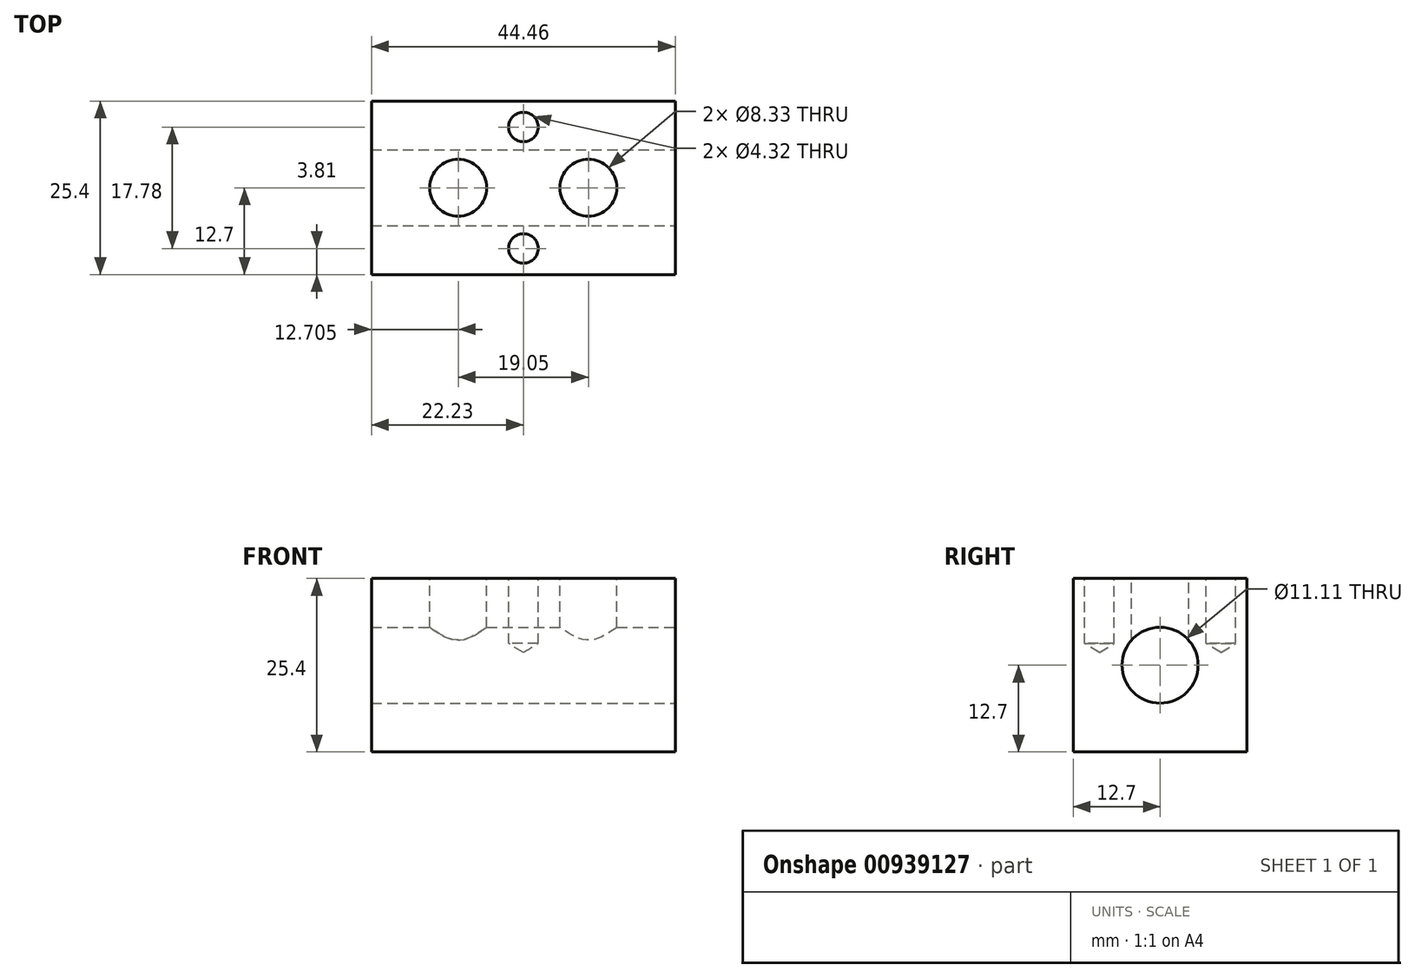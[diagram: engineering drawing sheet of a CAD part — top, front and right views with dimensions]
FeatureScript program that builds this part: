
annotation { "Feature Type Name" : "Feature", "Feature Type Description" : "" }
export const myFeature = defineFeature(function(context is Context, id is Id, definition is map)
    precondition{}
    {
        {
            var Q0;
            Q0=qCreatedBy(makeId("Front.planeOp"),FACE);
            var sketch = newSketch(context, id + "F0", { "sketchPlane" : qUnion([Q0])});
            skLineSegment(sketch, "E0.bottom", {"start": v(22.23, 12.7) * mm, "end": v(-22.23, 12.7) * mm});
            skLineSegment(sketch, "E0.top", {"start": v(22.23, -12.7) * mm, "end": v(-22.23, -12.7) * mm});
            skLineSegment(sketch, "E0.left", {"start": v(22.23, 12.7) * mm, "end": v(22.23, -12.7) * mm});
            skLineSegment(sketch, "E0.right", {"start": v(-22.23, 12.7) * mm, "end": v(-22.23, -12.7) * mm});
            skPoint(sketch, "E0.middle", {"position": v(0, 0) * mm});
            skSolve(sketch);
        }
        {
            var Q0;
            Q0=makeQuery(id+"F0.imprint","IMPRINT",FACE,{"disambiguationData":[TD([[makeQuery(id+"F0.imprint","IMPRINT",EDGE,{"derivedFrom":sQuery(id+"F0.wireOp",EDGE,"E0.bottom")}),1.0]])]});
            extrude(context, id + "F1", {"entities" : qUnion([Q0]), "endBound" : BoundingType.SYMMETRIC, "depth" : 25.4 * mm, "offsetDistance" : 25.4 * mm});
        }
        {
            var Q0;
            Q0=makeQuery(id+"F1.opExtrude","SWEPT_FACE",FACE,{"disambiguationData":[OSD([sQuery(id+"F0.wireOp",EDGE,"E0.left")])]});
            var sketch = newSketch(context, id + "F2", { "sketchPlane" : qUnion([Q0])});
            skCircle(sketch, "E1", {"center": v(0, 0) * mm, "radius": 5.56 * mm});
            skSolve(sketch);
        }
        {
            var Q0;
            Q0=makeQuery(id+"F1.opExtrude","SWEPT_FACE",FACE,{"disambiguationData":[OSD([sQuery(id+"F0.wireOp",EDGE,"E0.bottom")])]});
            var sketch = newSketch(context, id + "F3", { "sketchPlane" : qUnion([Q0])});
            skCircle(sketch, "E2", {"center": v(-9.53, 0) * mm, "radius": 4.17 * mm});
            skPoint(sketch, "E2.centerSnap0", {"position": v(-22.23, 0) * mm});
            skCircle(sketch, "E3", {"center": v(9.53, 0) * mm, "radius": 4.17 * mm});
            skCircle(sketch, "E4", {"center": v(0, 8.9) * mm, "radius": 2.16 * mm});
            skPoint(sketch, "E4.centerSnap0", {"position": v(0, 12.7) * mm});
            skCircle(sketch, "E5", {"center": v(0, -8.9) * mm, "radius": 2.16 * mm});
            skSolve(sketch);
        }
        {
            var Q0;
            Q0=sQuery(id+"F3.wireOp",VERTEX,"E2.center");
            var Q1;
            Q1=makeQuery(id+"F1.opExtrude","SWEPT_BODY",BODY,{"disambiguationData":[OSD([sQuery(id+"F0.wireOp",EDGE,"E0.bottom"),sQuery(id+"F0.wireOp",EDGE,"E0.top"),sQuery(id+"F0.wireOp",EDGE,"E0.left"),sQuery(id+"F0.wireOp",EDGE,"E0.right")])]});
            hole(context, id + "F4", {"style" : HoleStyle.SIMPLE, "endStyle" : HoleEndStyle.BLIND, "holeDiameter" : 8.33 * mm, "majorDiameter" : 6.35 * mm, "holeDepth" : 12.7 * mm, "isTappedThrough" : true, "tappedDepth" : 12.7 * mm, "tapClearance" : 3, "locations" : qUnion([Q0]), "scope" : qUnion([Q1])});
        }
        {
            var Q0;
            Q0=sQuery(id+"F3.wireOp",VERTEX,"E3.center");
            var Q1;
            Q1=makeQuery(id+"F1.opExtrude","SWEPT_BODY",BODY,{"disambiguationData":[OSD([sQuery(id+"F0.wireOp",EDGE,"E0.bottom"),sQuery(id+"F0.wireOp",EDGE,"E0.top"),sQuery(id+"F0.wireOp",EDGE,"E0.left"),sQuery(id+"F0.wireOp",EDGE,"E0.right")])]});
            hole(context, id + "F5", {"style" : HoleStyle.SIMPLE, "endStyle" : HoleEndStyle.BLIND, "holeDiameter" : 8.33 * mm, "majorDiameter" : 6.35 * mm, "holeDepth" : 12.7 * mm, "isTappedThrough" : true, "tappedDepth" : 12.7 * mm, "tapClearance" : 3, "locations" : qUnion([Q0]), "scope" : qUnion([Q1])});
        }
        {
            var Q0;
            Q0=sQuery(id+"F3.wireOp",VERTEX,"E4.center");
            var Q1;
            Q1=sQuery(id+"F3.wireOp",VERTEX,"E5.center");
            var Q2;
            Q2=makeQuery(id+"F1.opExtrude","SWEPT_BODY",BODY,{"disambiguationData":[OSD([sQuery(id+"F0.wireOp",EDGE,"E0.bottom"),sQuery(id+"F0.wireOp",EDGE,"E0.top"),sQuery(id+"F0.wireOp",EDGE,"E0.left"),sQuery(id+"F0.wireOp",EDGE,"E0.right")])]});
            hole(context, id + "F6", {"style" : HoleStyle.SIMPLE, "endStyle" : HoleEndStyle.BLIND, "holeDiameter" : 4.32 * mm, "majorDiameter" : 6.35 * mm, "holeDepth" : 9.52 * mm, "isTappedThrough" : true, "tappedDepth" : 12.7 * mm, "tapClearance" : 3, "locations" : qUnion([Q0, Q1]), "scope" : qUnion([Q2])});
        }
        {
            var Q0;
            Q0=sQuery(id+"F2.wireOp",VERTEX,"E1.center");
            var Q1;
            Q1=makeQuery(id+"F1.opExtrude","SWEPT_BODY",BODY,{"disambiguationData":[OSD([sQuery(id+"F0.wireOp",EDGE,"E0.bottom"),sQuery(id+"F0.wireOp",EDGE,"E0.top"),sQuery(id+"F0.wireOp",EDGE,"E0.left"),sQuery(id+"F0.wireOp",EDGE,"E0.right")])]});
            hole(context, id + "F7", {"style" : HoleStyle.SIMPLE, "endStyle" : HoleEndStyle.THROUGH, "holeDiameter" : 11.1 * mm, "majorDiameter" : 6.35 * mm, "isTappedThrough" : true, "tappedDepth" : 12.7 * mm, "tapClearance" : 3, "locations" : qUnion([Q0]), "scope" : qUnion([Q1])});
        }
    });
